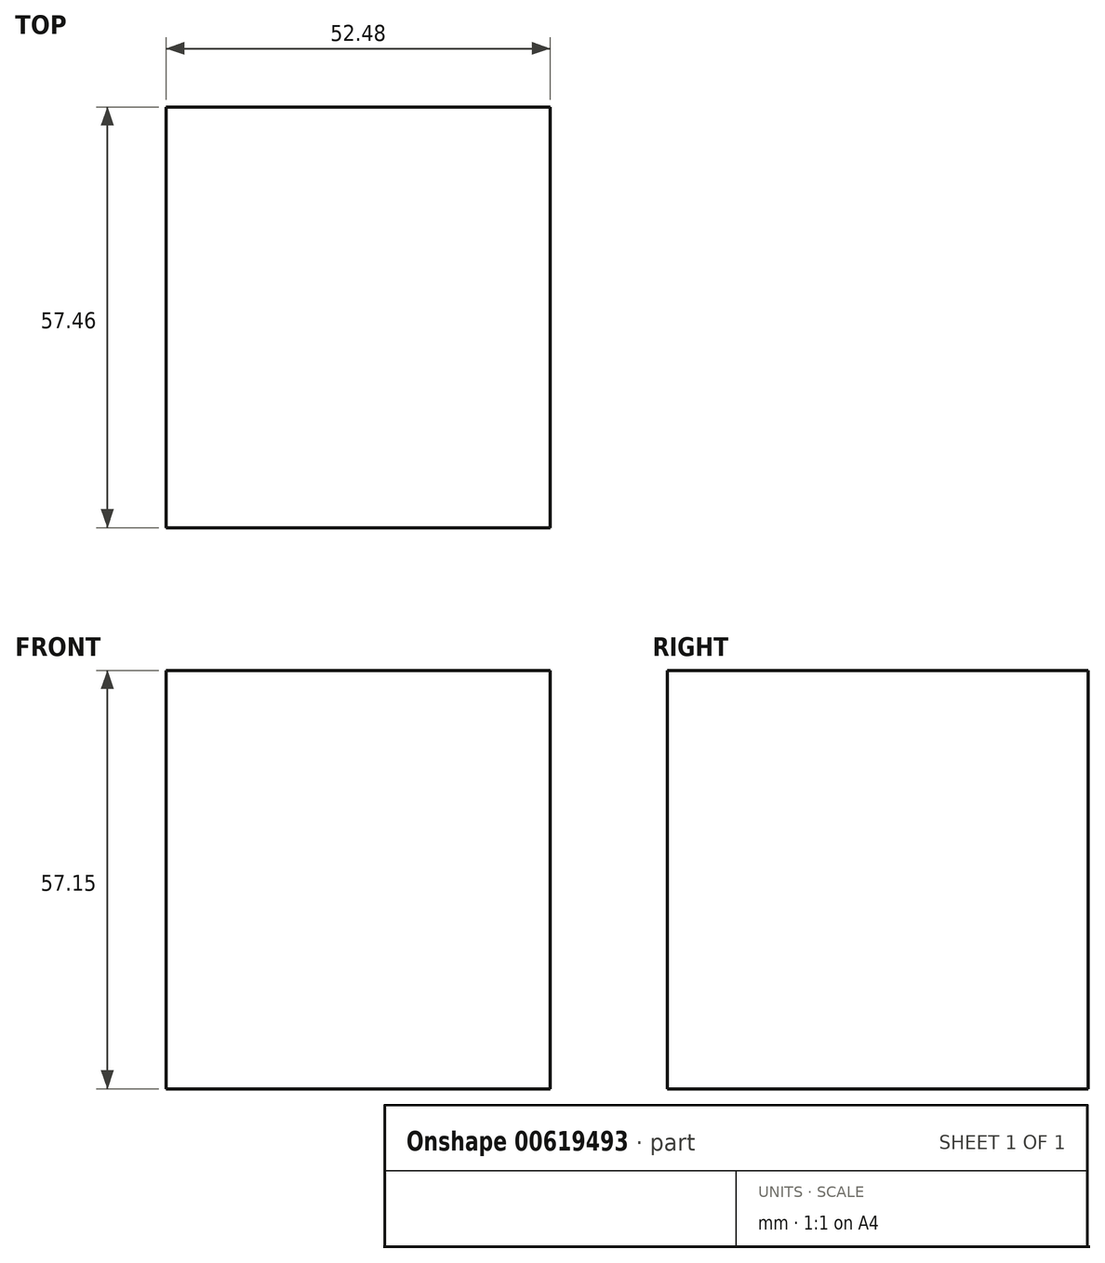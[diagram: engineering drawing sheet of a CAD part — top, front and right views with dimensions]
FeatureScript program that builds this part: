
annotation { "Feature Type Name" : "Feature", "Feature Type Description" : "" }
export const myFeature = defineFeature(function(context is Context, id is Id, definition is map)
    precondition{}
    {
        {
            var Q0;
            Q0=qCreatedBy(makeId("Top.planeOp"),FACE);
            var sketch = newSketch(context, id + "F0", { "sketchPlane" : qUnion([Q0])});
            skLineSegment(sketch, "E0.bottom", {"start": v(0, 0) * mm, "end": v(-52.48, 0) * mm});
            skLineSegment(sketch, "E0.top", {"start": v(0, 57.46) * mm, "end": v(-52.48, 57.46) * mm});
            skLineSegment(sketch, "E0.left", {"start": v(0, 0) * mm, "end": v(0, 57.46) * mm});
            skLineSegment(sketch, "E0.right", {"start": v(-52.48, 0) * mm, "end": v(-52.48, 57.46) * mm});
            skSolve(sketch);
        }
        {
            var Q0;
            Q0=makeQuery(id+"F0.imprint","IMPRINT",FACE,{"disambiguationData":[TD([[makeQuery(id+"F0.imprint","IMPRINT",EDGE,{"derivedFrom":sQuery(id+"F0.wireOp",EDGE,"E0.bottom")}),-1.0]])]});
            extrude(context, id + "F1", {"entities" : qUnion([Q0]), "depth" : 57.15 * mm, "offsetDistance" : 25.4 * mm});
        }
    });
